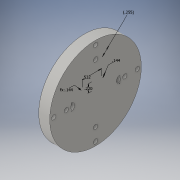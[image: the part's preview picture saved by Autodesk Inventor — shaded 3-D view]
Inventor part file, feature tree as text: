
AUTODESK INVENTOR PART (.ipt)
format: ipt  version: 2016 (Build 200138000, 138)  size: 183,296 bytes
history: native  units: in
note: dims shown in document units (in); Inventor stores cm internally (conversion verified against a paired STEP export)
features: sketch x7, extrude x3, revolve x1
ambient origin geometry x8: Origin, YZ Plane, XZ Plane, XY Plane, X Axis, Y Axis, Z Axis, Center Point
bodies: Solid1 (feature_tree)
feature tree (11):
  revolve  "Revolution1"  [1 undecoded]
  extrude  "Extrusion1"  Depth=0.105in
  sketch  "Sketch3"  dims[d4=0.105in d5=0.255in]
  sketch  "Sketch4"  dims[d6=0.2in d7=0.1in]
  extrude  "Extrusion2"  Depth=0.105in
  sketch  "Sketch5"  dims[d8=90.0deg]
  extrude  "Extrusion3"  Depth=0.1in
  sketch  "Sketch7"  dims[d10=1.5748in d12=360.0deg d14=0.5in d15=0.0in d16=0.255in d17=0.1275in d18=0.1181in d19=1.5748in d21=360.0deg d23=0.2in d24=0.0in d25=1.14in d26=0.787in d27=0.2in d28=0.2in d29=0.5in d30=0.0in d31=0.144in d32=0.144in d33=0.532in d34=0.22in]
  sketch  "Sketch1"  dims[d0=1.2499in d1=0.3in]
  sketch  "Sketch2"  dims[d2=0.22in d3=0.105in]
  sketch  "Sketch6"  dims[d9=0.1181in]
note: 1 required parameter value undecoded (feature->parameter linkage not recoverable at this tier; creation-order binding heuristic only, values carry confidence <= 0.55)
